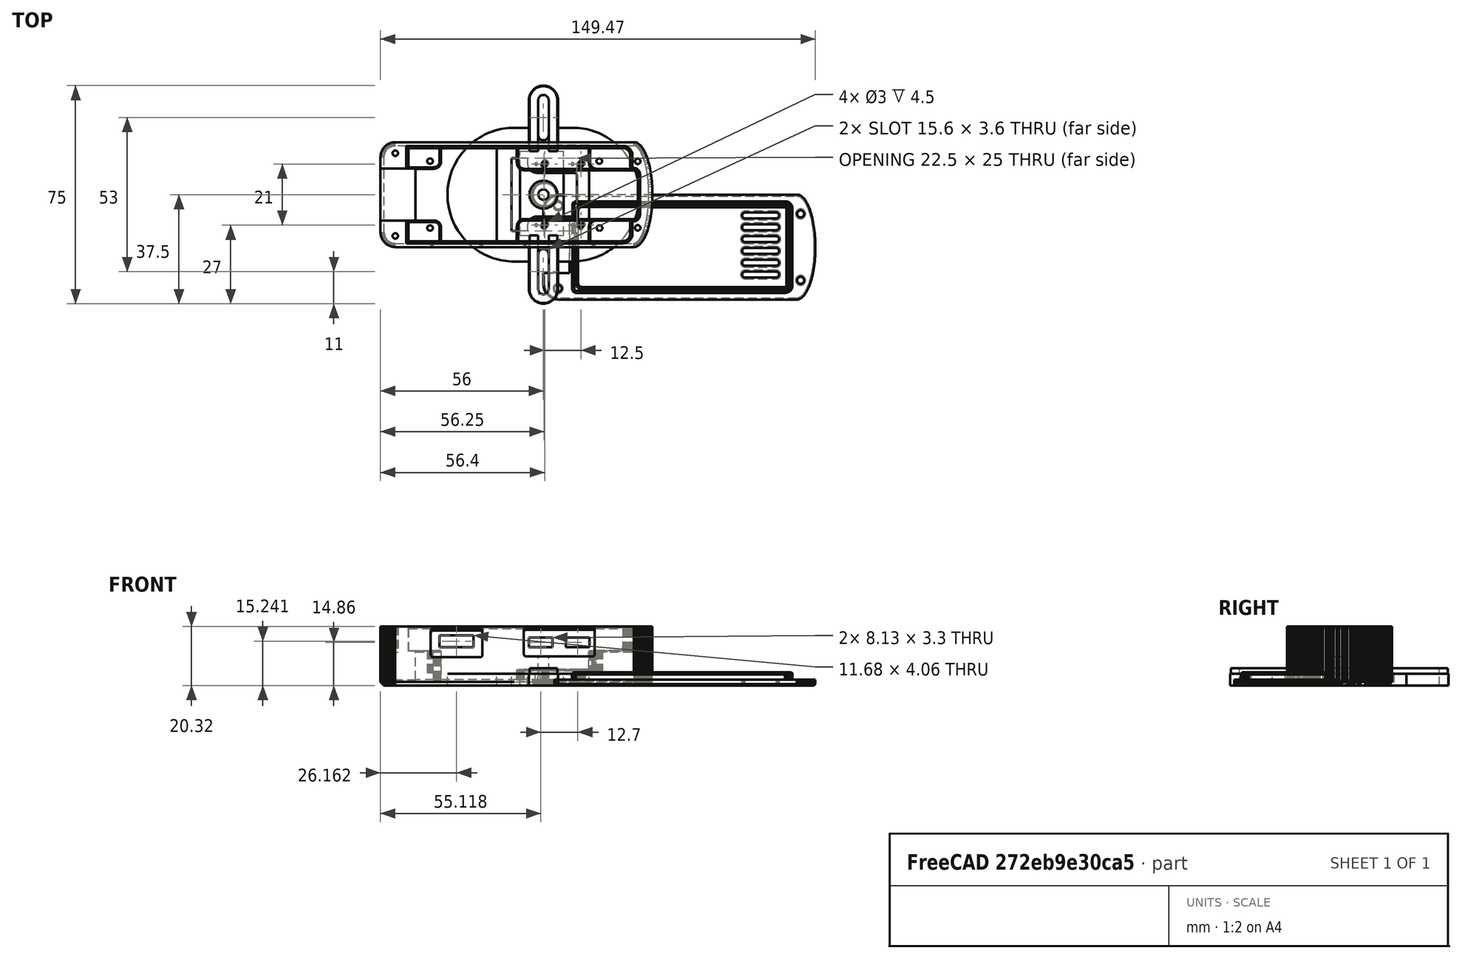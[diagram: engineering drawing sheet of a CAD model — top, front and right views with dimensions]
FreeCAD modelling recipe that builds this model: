
FCSTD DOCUMENT  (FreeCAD 0.19R23578 (Git))
Label: pizerohingedcasecamera
License: All rights reserved
LicenseURL: http://en.wikipedia.org/wiki/All_rights_reserved
objects: Part::Box×9, Part::Cylinder×7, Part::MultiFuse×6, Part::FeaturePython×5, Part::Cut×5, App::Part×4, Part::Feature×3, Part::Compound×2, PartDesign::ShapeBinder×1, Sketcher::SketchObject×1, PartDesign::Pad×1, PartDesign::Body×1, Part::Mirroring×1
note: 38 computed .brp shape members not serialized (recipe doc carries the construction recipe); baked Part::Feature solids carry a one-line shape summary decoded from their .brp

FEATURE [Part::Cylinder] Cylinder004  label="bolt hole"
  Angle = 360
  AttacherType = Attacher::AttachEngine3D
  Height = 10
  Radius = 1.8
FEATURE [Part::FeaturePython] Array  label="bolt hole array"  # Draft array (typed FeaturePython)
  Angle = 360
  ArrayType = 0
  Axis = (0,0,1)
  Base = -> Cylinder004
  Center = (0,0,0)
  Count = 2
  ExpandArray = false
  Fuse = false
  IntervalAxis = (0,0,0)
  IntervalX = (100,0,0)
  IntervalY = (0,65,0)
  IntervalZ = (0,0,100)
  NumberCircles = 3
  NumberPolar = 5
  NumberX = 1
  NumberY = 2
  NumberZ = 1
  Placement = pos=(0,-32.5,0) rot=(0,0,1;0rad)
  PlacementList = 2 placements: [(0,0,0),(0,65,0)]
  RadialDistance = 50
  ScaleList = (2) [(1,1,1),(1,1,1)]
  Symmetry = 1
  TangentialDistance = 25
  expr: .Placement.Base.y = -.IntervalY.y / 2
FEATURE [Part::Box] Box002  label="Cube002"
  AttacherType = Attacher::AttachEngine3D
  Height = 10
  Length = 3.6
  Placement = pos=(-1.8,-32.5,0) rot=(0,0,1;0rad)
  Width = 65
  expr: .Placement.Base.x = -Length / 2
  expr: Length = <<bolt hole>>.Radius * 2
  expr: .Placement.Base.y = -Width / 2
  expr: Width = <<bolt hole array>>.IntervalY.y
FEATURE [Part::MultiFuse] Fusion003  label="bolt hole fusion"
  Shapes = -> [Array,Box002]
FEATURE [Part::Box] Box003  label="wall cube"
  AttacherType = Attacher::AttachEngine3D
  Height = 4
  Length = 9.6
  Placement = pos=(-4.8,-32.5,0) rot=(0,0,1;0rad)
  Width = 65
  expr: Height = <<bolt wall>>.Height
  expr: Width = <<bolt wall array>>.IntervalY.y
  expr: .Placement.Base.y = -Width / 2
  expr: Length = <<bolt wall>>.Radius * 2
  expr: .Placement.Base.x = -Length / 2
FEATURE [Part::Cylinder] Cylinder005  label="bolt wall"
  Angle = 360
  AttacherType = Attacher::AttachEngine3D
  Height = 4
  Radius = 4.8
  expr: Radius = <<bolt hole>>.Radius + 3mm
FEATURE [Part::FeaturePython] Array001  label="bolt wall array"  # Draft array (typed FeaturePython)
  Angle = 360
  ArrayType = 0
  Axis = (0,0,1)
  Base = -> Cylinder005
  Center = (0,0,0)
  Count = 2
  ExpandArray = false
  Fuse = false
  IntervalAxis = (0,0,0)
  IntervalX = (100,0,0)
  IntervalY = (0,65,0)
  IntervalZ = (0,0,100)
  NumberCircles = 3
  NumberPolar = 5
  NumberX = 1
  NumberY = 2
  NumberZ = 1
  Placement = pos=(0,-32.5,0) rot=(0,0,1;0rad)
  PlacementList = 2 placements: [(0,0,0),(0,65,0)]
  RadialDistance = 50
  ScaleList = (2) [(1,1,1),(1,1,1)]
  Symmetry = 1
  TangentialDistance = 25
  expr: .Placement.Base.y = -.IntervalY.y / 2
FEATURE [PartDesign::ShapeBinder] ShapeBinder
  TraceSupport = false
FEATURE [Sketcher::SketchObject] Sketch018
  MapMode = 5
  Support = -> [XY_Plane005]
  sketch-geometry (36):
    g0: LineSegment StartX=10.4776 StartY=-7.5 StartZ=0 EndX=-2.1829 EndY=-7.5 EndZ=0
    g1: LineSegment StartX=-5.5 StartY=-12.5 StartZ=0 EndX=-11 EndY=-12.5 EndZ=0
    g2: LineSegment StartX=-11 StartY=12.5 StartZ=0 EndX=-11 EndY=-12.5 EndZ=0
    g3: LineSegment StartX=-5.5 StartY=12.5 StartZ=0 EndX=-11 EndY=12.5 EndZ=0
    g4: LineSegment StartX=-5.5 StartY=12.5 StartZ=0 EndX=-5.5 EndY=10.8171 EndZ=0
    g5: LineSegment StartX=-2.1829 StartY=7.5 StartZ=0 EndX=10.4776 EndY=7.5 EndZ=0
    g6: Circle CenterX=-2.49941 CenterY=10.498 CenterZ=0 NormalX=0 NormalY=0 NormalZ=1 AngleXU=0 Radius=0.5
    g7: Circle CenterX=10.0006 CenterY=10.5207 CenterZ=0 NormalX=0 NormalY=0 NormalZ=1 AngleXU=0 Radius=0.5
    g8: Circle CenterX=10 CenterY=-10.4793 CenterZ=0 NormalX=0 NormalY=0 NormalZ=1 AngleXU=0 Radius=0.5
    g9: Circle CenterX=-2.5 CenterY=-10.502 CenterZ=0 NormalX=0 NormalY=0 NormalZ=1 AngleXU=0 Radius=0.5
    g10: LineSegment StartX=15.68 StartY=17 StartZ=0 EndX=15.68 EndY=-17 EndZ=0
    g11: LineSegment StartX=-16 StartY=-17 StartZ=0 EndX=-16 EndY=17 EndZ=0
    g12: LineSegment StartX=-5.5 StartY=-10.8171 StartZ=0 EndX=-5.5 EndY=-12.5 EndZ=0
    g13: LineSegment StartX=11.5 StartY=6.47757 StartZ=0 EndX=11.5 EndY=-6.47757 EndZ=0
    g14: ArcOfCircle CenterX=10.4776 CenterY=-6.47757 CenterZ=0 NormalX=0 NormalY=0 NormalZ=1 AngleXU=0 Radius=1.02243 StartAngle=4.71239 EndAngle=6.28319
    g15: ArcOfCircle CenterX=10.4776 CenterY=6.47757 CenterZ=0 NormalX=0 NormalY=0 NormalZ=1 AngleXU=0 Radius=1.02243 StartAngle=0 EndAngle=1.5708
    g16: ArcOfCircle CenterX=-2.1829 CenterY=-10.8171 CenterZ=0 NormalX=0 NormalY=0 NormalZ=1 AngleXU=0 Radius=3.3171 StartAngle=1.5708 EndAngle=3.14159
    g17: ArcOfCircle CenterX=-2.1829 CenterY=10.8171 CenterZ=0 NormalX=0 NormalY=0 NormalZ=1 AngleXU=0 Radius=3.3171 StartAngle=3.14159 EndAngle=4.71239
    g18: LineSegment StartX=-16 StartY=17 StartZ=0 EndX=-5 EndY=17 EndZ=0
    g19: LineSegment StartX=-5 StartY=17 StartZ=0 EndX=-5 EndY=32.5 EndZ=0
    g20: LineSegment StartX=15.68 StartY=17 StartZ=0 EndX=5 EndY=17 EndZ=0
    g21: LineSegment StartX=5 StartY=17 StartZ=0 EndX=5 EndY=32.5 EndZ=0
    g22: ArcOfCircle CenterX=2e-16 CenterY=32.5 CenterZ=0 NormalX=0 NormalY=0 NormalZ=1 AngleXU=0 Radius=5 StartAngle=5e-16 EndAngle=3.14159
    g23: LineSegment StartX=-16 StartY=-17 StartZ=0 EndX=-5 EndY=-17 EndZ=0
    g24: LineSegment StartX=-5 StartY=-17 StartZ=0 EndX=-5 EndY=-32.5 EndZ=0
    g25: LineSegment StartX=15.68 StartY=-17 StartZ=0 EndX=5 EndY=-17 EndZ=0
    g26: LineSegment StartX=5 StartY=-17 StartZ=0 EndX=5 EndY=-32.5 EndZ=0
    g27: ArcOfCircle CenterX=1e-16 CenterY=-32.5 CenterZ=0 NormalX=0 NormalY=0 NormalZ=1 AngleXU=0 Radius=5 StartAngle=3.14159 EndAngle=6.28319
    g28: LineSegment StartX=-1.8 StartY=-20.5 StartZ=0 EndX=-1.8 EndY=-32.5 EndZ=0
    g29: LineSegment StartX=1.8 StartY=-20.5 StartZ=0 EndX=1.8 EndY=-32.5 EndZ=0
    g30: ArcOfCircle CenterX=1e-16 CenterY=-20.5 CenterZ=0 NormalX=0 NormalY=0 NormalZ=1 AngleXU=0 Radius=1.8 StartAngle=0 EndAngle=3.14159
    g31: ArcOfCircle CenterX=1e-16 CenterY=-32.5 CenterZ=0 NormalX=0 NormalY=0 NormalZ=1 AngleXU=0 Radius=1.8 StartAngle=3.14159 EndAngle=6.28319
    g32: LineSegment StartX=-1.8 StartY=32.5 StartZ=0 EndX=-1.8 EndY=20.5 EndZ=0
    g33: LineSegment StartX=1.8 StartY=32.5 StartZ=0 EndX=1.8 EndY=20.5 EndZ=0
    g34: ArcOfCircle CenterX=1e-16 CenterY=32.5 CenterZ=0 NormalX=0 NormalY=0 NormalZ=1 AngleXU=0 Radius=1.8 StartAngle=-9e-16 EndAngle=3.14159
    g35: ArcOfCircle CenterX=-1e-16 CenterY=20.5 CenterZ=0 NormalX=0 NormalY=0 NormalZ=1 AngleXU=0 Radius=1.8 StartAngle=3.14159 EndAngle=6.28319
  constraints (93):
    c: Vertical(g4)
    c: Radius(g9) = 0.5
    c: Equal(g9,g8)
    c: Equal(g8,g7)
    c: Equal(g7,g6)
    c: DistanceX(g6,g7) = 12.5
    c: DistanceX(g9,g8) = 12.5
    c: DistanceY(g9,g6) = 21
    c: DistanceY(g8,g7) = 21
    c: Vertical(g2)
    c: Vertical(g11)
    c: Horizontal(g5)
    c: Horizontal(g0)
    c: Equal(g1,g3)
    c: Equal(g5,g0)
    c: Coincident(g4,g3)
    c: Coincident(g3,g2)
    c: Horizontal(g3)
    c: Coincident(g2,g1)
    c: Horizontal(g1)
    c: Vertical(g10)
    c: Coincident(g12,g1)
    c: Vertical(g12)
    c: Tangent(g0,g14) = 1.5708
    c: Tangent(g13,g14) = 1.5708
    c: Tangent(g5,g15) = 1.5708
    c: Tangent(g13,g15) = 1.5708
    c: Vertical(g13)
    c: DistanceX(g-1,g13) = 11.5
    c: DistanceY(g-1,g5) = 7.5
    c: DistanceX(g-1,g8) = 10
    c: DistanceY(g0,g-1) = 7.5
    c: DistanceY(g1,g-1) = 12.5
    c: DistanceY(g-1,g3) = 12.5
    c: DistanceX(g2,g-1) = 11
    c: DistanceX(g1,g-1) = 5.5
    c: Tangent(g12,g16) = -1.5708
    c: Tangent(g0,g16) = -1.5708
    c: Tangent(g4,g17) = -1.5708
    c: Tangent(g5,g17) = -1.5708
    c: Equal(g17,g16)
    c: Coincident(g18,g11)
    c: Horizontal(g18)
    c: Coincident(g19,g18)
    c: Vertical(g19)
    c: Coincident(g20,g10)
    c: Horizontal(g20)
    c: Coincident(g21,g20)
    c: Vertical(g21)
    c: Symmetric(g20,g18,g-2)
    c: Coincident(g22,g19)
    c: Equal(g21,g19)
    c: DistanceX(g18,g-1) = 5
    c: Coincident(g23,g11)
    c: Horizontal(g23)
    c: Coincident(g24,g23)
    c: Vertical(g24)
    c: Coincident(g25,g10)
    c: Horizontal(g25)
    c: Coincident(g26,g25)
    c: Symmetric(g26,g24,g-2)
    c: DistanceX(g24,g-1) = 5
    c: Coincident(g27,g24)
    c: Tangent(g27,g26) = 1.5708
    c: DistanceY(g27,g22) = 65
    c: Tangent(g22,g21) = -1.5708
    c: DistanceY(g27,g-1) = 32.5
    c: DistanceX(g11,g-1) = 16
    c: DistanceY(g-1,g11) = 17
    c: DistanceY(g11,g-1) = 17
    c: Vertical(g28)
    c: Vertical(g29)
    c: Symmetric(g28,g29,g-2)
    c: Equal(g29,g28)
    c: DistanceX(g28,g29) = 3.6
    c: Coincident(g30,g29)
    c: DistanceY(g29,g26) = 0
    c: DistanceY(g28,g28) = 12
    c: Tangent(g30,g28) = -1.5708
    c: Coincident(g31,g28)
    c: Tangent(g31,g29) = 1.5708
    c: Vertical(g32)
    c: Vertical(g33)
    c: Equal(g33,g32)
    c: DistanceX(g32,g33) = 3.6
    c: Coincident(g34,g33)
    c: DistanceY(g32,g32) = 12
    c: Tangent(g34,g32) = -1.5708
    c: Coincident(g35,g32)
    c: Tangent(g35,g33) = 1.5708
    c: DistanceY(g21,g33) = 0
    c: Symmetric(g32,g33,g-2)
    c: Symmetric(g23,g25,g-2)
FEATURE [PartDesign::Pad] Pad006
  Direction = (1,1,1)
  Length = 4
  Length2 = 100
  Profile = -> Sketch018
  Type = 0
FEATURE [PartDesign::Body] Body001
  Group = -> [ShapeBinder,Sketch018,Pad006]
  Origin = -> Origin005
  Tip = -> Pad006
FEATURE [App::Part] Part003  label="microscope adapter part"
  Group = -> [Body001]
  Origin = -> Origin004
FEATURE [Part::Box] Box004  label="extract cube"
  AttacherType = Attacher::AttachEngine3D
  Height = 10
  Length = 15
  Placement = pos=(-8,-14,0) rot=(0,0,1;0rad)
  Width = 29
FEATURE [Part::MultiFuse] Fusion005  label="extract fusion"
  Shapes = -> [Box004,Fusion003]
FEATURE [Part::Feature] Pi_Zero_Case_Arm_Mount001001001
  Placement = pos=(-72,18.05,0) rot=(0,0,-1;1.5708rad)
  shape: bbox 109.5 x 36.07 x 20.32 mm, 7722 faces, 0 solids (baked)
FEATURE [Part::Cylinder] Cylinder006  label="cover cylinder"
  Angle = 180
  AttacherType = Attacher::AttachEngine3D
  Height = 4
  Placement = pos=(10,0,0) rot=(0,0,-1;1.5708rad)
  Radius = 23
  expr: Height = <<bolt wall>>.Height
FEATURE [Part::Box] Box005  label="intercylinder fill cube"
  AttacherType = Attacher::AttachEngine3D
  Height = 4
  Length = 20
  Placement = pos=(-10,-23,0) rot=(0,0,1;0rad)
  Width = 46
  expr: .Placement.Base.x = -Length / 2
  expr: .Placement.Base.y = -Width / 2
  expr: Width = <<cover cylinder>>.Radius * 2
  expr: Length = <<cover cylinder>>.Placement.Base.x * 2
  expr: Height = <<bolt wall>>.Height
FEATURE [Part::Mirroring] Part__Mirroring  label="cover cylinder (Mirror #1)"
  Base = (0,0,0)
  Normal = (1,0,0)
  Source = -> Cylinder006
FEATURE [Part::MultiFuse] Fusion004  label="bolt wall fusion"
  Shapes = -> [Array001,Box003,Box005,Part__Mirroring,Cylinder006]
FEATURE [Part::Cut] Cut001  label="microscope attachment cut"
  Base = -> Fusion004
  Tool = -> Fusion005
FEATURE [App::Part] Part  label="microscope asdapter attachment"
  Group = -> [Cut001]
  Origin = -> Origin
FEATURE [Part::Compound] Compound  label="RPI compound"
  Links = -> [Cut001,Pi_Zero_Case_Arm_Mount001001001]
FEATURE [Part::Cylinder] Cylinder008  label="bolt hole001"
  Angle = 360
  AttacherType = Attacher::AttachEngine3D
  Height = 10
  Radius = 1.8
FEATURE [Part::FeaturePython] Array002  label="bolt hole array001"  # Draft array (typed FeaturePython)
  Angle = 360
  ArrayType = 0
  Axis = (0,0,1)
  Base = -> Cylinder008
  Center = (0,0,0)
  Count = 2
  ExpandArray = false
  Fuse = false
  IntervalAxis = (0,0,0)
  IntervalX = (100,0,0)
  IntervalY = (0,65,0)
  IntervalZ = (0,0,100)
  NumberCircles = 3
  NumberPolar = 5
  NumberX = 1
  NumberY = 2
  NumberZ = 1
  Placement = pos=(0,-32.5,0) rot=(0,0,1;0rad)
  PlacementList = 2 placements: [(0,0,0),(0,65,0)]
  RadialDistance = 50
  ScaleList = (2) [(1,1,1),(1,1,1)]
  Symmetry = 1
  TangentialDistance = 25
  expr: .Placement.Base.y = -.IntervalY.y / 2
FEATURE [Part::Box] Box006  label="Cube003"
  AttacherType = Attacher::AttachEngine3D
  Height = 10
  Length = 3.6
  Placement = pos=(-1.8,-32.5,0) rot=(0,0,1;0rad)
  Width = 65
  expr: Width = <<bolt hole array001>>.IntervalY.y
  expr: .Placement.Base.y = -Width / 2
  expr: Length = <<bolt hole001>>.Radius * 2
  expr: .Placement.Base.x = -Length / 2
FEATURE [Part::MultiFuse] Fusion007  label="bolt hole fusion001"
  Shapes = -> [Array002,Box006]
FEATURE [Part::Cylinder] Cylinder009  label="bolt wall001"
  Angle = 360
  AttacherType = Attacher::AttachEngine3D
  Height = 6
  Radius = 4.8
  expr: Radius = <<bolt hole001>>.Radius + 3mm
FEATURE [Part::FeaturePython] Array003  label="bolt wall array001"  # Draft array (typed FeaturePython)
  Angle = 360
  ArrayType = 0
  Axis = (0,0,1)
  Base = -> Cylinder009
  Center = (0,0,0)
  Count = 2
  ExpandArray = false
  Fuse = false
  IntervalAxis = (0,0,0)
  IntervalX = (100,0,0)
  IntervalY = (0,65,0)
  IntervalZ = (0,0,100)
  NumberCircles = 3
  NumberPolar = 5
  NumberX = 1
  NumberY = 2
  NumberZ = 1
  Placement = pos=(0,-32.5,0) rot=(0,0,1;0rad)
  PlacementList = 2 placements: [(0,0,0),(0,65,0)]
  RadialDistance = 50
  ScaleList = (2) [(1,1,1),(1,1,1)]
  Symmetry = 1
  TangentialDistance = 25
  expr: .Placement.Base.y = -.IntervalY.y / 2
FEATURE [Part::Box] Box007  label="extract cube001"
  AttacherType = Attacher::AttachEngine3D
  Height = 10
  Length = 15
  Placement = pos=(-8,-14,0) rot=(0,0,1;0rad)
  Width = 29
FEATURE [Part::MultiFuse] Fusion006  label="extract fusion001"
  Shapes = -> [Box007,Fusion007]
FEATURE [Part::Box] Box009  label="wall cube001"
  AttacherType = Attacher::AttachEngine3D
  Height = 6
  Length = 9.6
  Placement = pos=(-4.8,-32.5,0) rot=(0,0,1;0rad)
  Width = 65
  expr: .Placement.Base.x = -Length / 2
  expr: Length = <<bolt wall001>>.Radius * 2
  expr: .Placement.Base.y = -Width / 2
  expr: Width = <<bolt wall array001>>.IntervalY.y
  expr: Height = <<bolt wall001>>.Height
FEATURE [Part::MultiFuse] Fusion008  label="bolt wall fusion001"
  Shapes = -> [Array003,Box009]
FEATURE [Part::Cut] Cut002002  label="microscope attachment cut001"
  Base = -> Fusion008
  Tool = -> Fusion006
FEATURE [Part::Cylinder] Cylinder010  label="hole narrowing fill"
  Angle = 360
  AttacherType = Attacher::AttachEngine3D
  Height = 4.5
  Placement = pos=(0.4,-10.5,0) rot=(0,0,1;0rad)
  Radius = 1.5
FEATURE [Part::Cylinder] Cylinder011  label="hole narrowing hole"
  Angle = 360
  AttacherType = Attacher::AttachEngine3D
  Height = 10
  Placement = pos=(0.4,-10.5,0) rot=(0,0,1;0rad)
  Radius = 0.5
FEATURE [Part::Cut] Cut002003  label="hole narrowing cut"
  Base = -> Cylinder010
  Placement = pos=(0,0,1) rot=(0,0,1;0rad)
  Tool = -> Cylinder011
FEATURE [Part::FeaturePython] Array004  label="hole narrowing array"  # Draft array (typed FeaturePython)
  Angle = 360
  ArrayType = 0
  Axis = (0,0,1)
  Base = -> Cut002003
  Center = (0,0,0)
  Count = 4
  ExpandArray = false
  Fuse = false
  IntervalAxis = (0,0,0)
  IntervalX = (12.5,0,0)
  IntervalY = (0,21,0)
  IntervalZ = (0,0,100)
  NumberCircles = 3
  NumberPolar = 5
  NumberX = 2
  NumberY = 2
  NumberZ = 1
  PlacementList = 4 placements: [(0,0,1),(0,21,1),(12.5,0,1),(12.5,21,1)]
  RadialDistance = 50
  ScaleList = (4) [(1,1,1),(1,1,1),(1,1,1),(1,1,1)]
  Symmetry = 1
  TangentialDistance = 25
FEATURE [Part::Box] Box010  label="remove arm cube"
  AttacherType = Attacher::AttachEngine3D
  Height = 23
  Length = 35
  Placement = pos=(-79,-9,2) rot=(0,0,1;0rad)
  Width = 18
FEATURE [Part::Feature] Pi_Zero_Case_Arm_Mount001001002_solid  label="Pi_Zero_Case_Arm_Mount001001002 (Solid)"
  shape: bbox 109.5 x 36.07 x 20.32 mm, 7722 faces (baked)
FEATURE [Part::Compound] Compound001  label="RPI compound001"
  Links = -> [Cut002002,Array004,Pi_Zero_Case_Arm_Mount001001002_solid]
FEATURE [Part::Cut] Cut002004  label="Pi_Zero_Case"
  Base = -> Compound001
  Tool = -> Box010
FEATURE [Part::Feature] Pi_Zero_Case_Cover_Vented_2001001_solid  label="Pi_Zero_Case_Cover_Vented_2001001 (Solid)"
  Placement = pos=(0,0,0) rot=(0,0,-1;1.5708rad)
  shape: bbox 93.47 x 36.07 x 7.112 mm, 6382 faces (baked)
FEATURE [Part::Box] Box011  label="remove arm cube001"
  AttacherType = Attacher::AttachEngine3D
  Height = 23
  Length = 35
  Placement = pos=(-26,-27,-10) rot=(0,0,1;0rad)
  Width = 18
FEATURE [App::Part] Part004  label="Pi Zero Case Part"
  Group = -> [Cut002004]
  Origin = -> Origin006
FEATURE [Part::Cut] Cut  label="Pi Zero Case Cover Cut"
  Base = -> Pi_Zero_Case_Cover_Vented_2001001_solid
  Tool = -> Box011
FEATURE [App::Part] Part005  label="Pi Zero Case Cover Part"
  Group = -> [Cut]
  Origin = -> Origin007
  Placement = pos=(-57,-18,22) rot=(1,0,0;3.14159rad)
